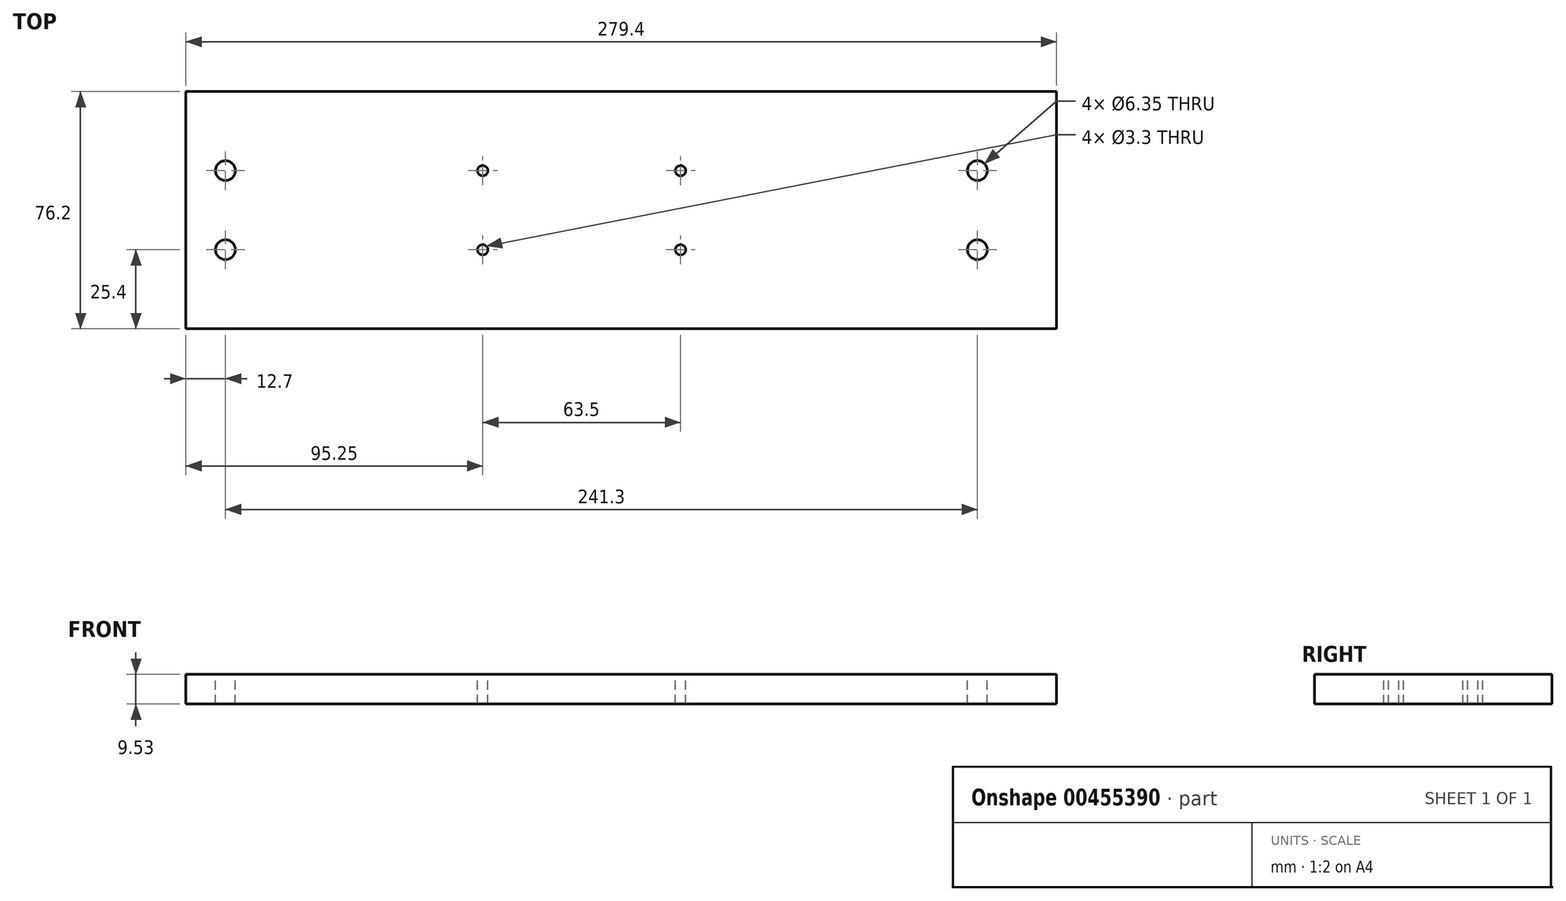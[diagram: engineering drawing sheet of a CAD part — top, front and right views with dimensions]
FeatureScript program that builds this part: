
annotation { "Feature Type Name" : "Feature", "Feature Type Description" : "" }
export const myFeature = defineFeature(function(context is Context, id is Id, definition is map)
    precondition{}
    {
        {
            var Q0;
            Q0=qCreatedBy(makeId("Top.planeOp"),FACE);
            var sketch = newSketch(context, id + "F0", { "sketchPlane" : qUnion([Q0])});
            skLineSegment(sketch, "E0.bottom", {"start": v(-139.7, 38.1) * mm, "end": v(139.7, 38.1) * mm});
            skLineSegment(sketch, "E0.top", {"start": v(-139.7, -38.1) * mm, "end": v(139.7, -38.1) * mm});
            skLineSegment(sketch, "E0.left", {"start": v(-139.7, 38.1) * mm, "end": v(-139.7, -38.1) * mm});
            skLineSegment(sketch, "E0.right", {"start": v(139.7, 38.1) * mm, "end": v(139.7, -38.1) * mm});
            skLineSegment(sketch, "E1", {"start": v(-113.57, 0) * mm, "end": v(160.82, 0) * mm, "construction": true});
            skSolve(sketch);
        }
        {
            var Q0;
            Q0=qSketchRegion(id+"F0",true);
            extrude(context, id + "F1", {"entities" : qUnion([Q0]), "depth" : 9.52 * mm});
        }
        {
            var Q0;
            Q0=makeQuery(id+"F1.opExtrude","CAP_FACE",FACE,{"disambiguationData":[OSD([sQuery(id+"F0.wireOp",EDGE,"E0.bottom"),sQuery(id+"F0.wireOp",EDGE,"E0.top"),sQuery(id+"F0.wireOp",EDGE,"E0.left"),sQuery(id+"F0.wireOp",EDGE,"E0.right")])],"isStart":false});
            var sketch = newSketch(context, id + "F2", { "sketchPlane" : qUnion([Q0])});
            skLineSegment(sketch, "E2", {"start": v(-168.91, 0) * mm, "end": v(166.69, 0) * mm, "construction": true});
            skCircle(sketch, "E3", {"center": v(-127, 12.7) * mm, "radius": 3.17 * mm});
            skCircle(sketch, "E4.MirrorC", {"center": v(-127, -12.7) * mm, "radius": 3.17 * mm});
            skCircle(sketch, "E5", {"center": v(-44.45, 12.7) * mm, "radius": 1.65 * mm});
            skCircle(sketch, "E6.MirrorC", {"center": v(-44.45, -12.7) * mm, "radius": 1.65 * mm});
            skCircle(sketch, "E7.1.0.0", {"center": v(19.05, 12.7) * mm, "radius": 1.65 * mm});
            skCircle(sketch, "E7.1.0.1", {"center": v(19.05, -12.7) * mm, "radius": 1.65 * mm});
            skLineSegment(sketch, "E7.direction1", {"start": v(-44.45, 12.7) * mm, "end": v(19.05, 12.7) * mm, "construction": true});
            skCircle(sketch, "E8", {"center": v(114.3, 12.7) * mm, "radius": 3.18 * mm});
            skCircle(sketch, "E9.MirrorC", {"center": v(114.3, -12.7) * mm, "radius": 3.18 * mm});
            skSolve(sketch);
        }
        {
            var Q0;
            Q0=qSketchRegion(id+"F2",true);
            extrude(context, id + "F3", {"entities" : qUnion([Q0]), "operationType" : NewBodyOperationType.REMOVE, "endBound" : BoundingType.THROUGH_ALL, "oppositeDirection" : true, "depth" : 25.4 * mm});
        }
    });
